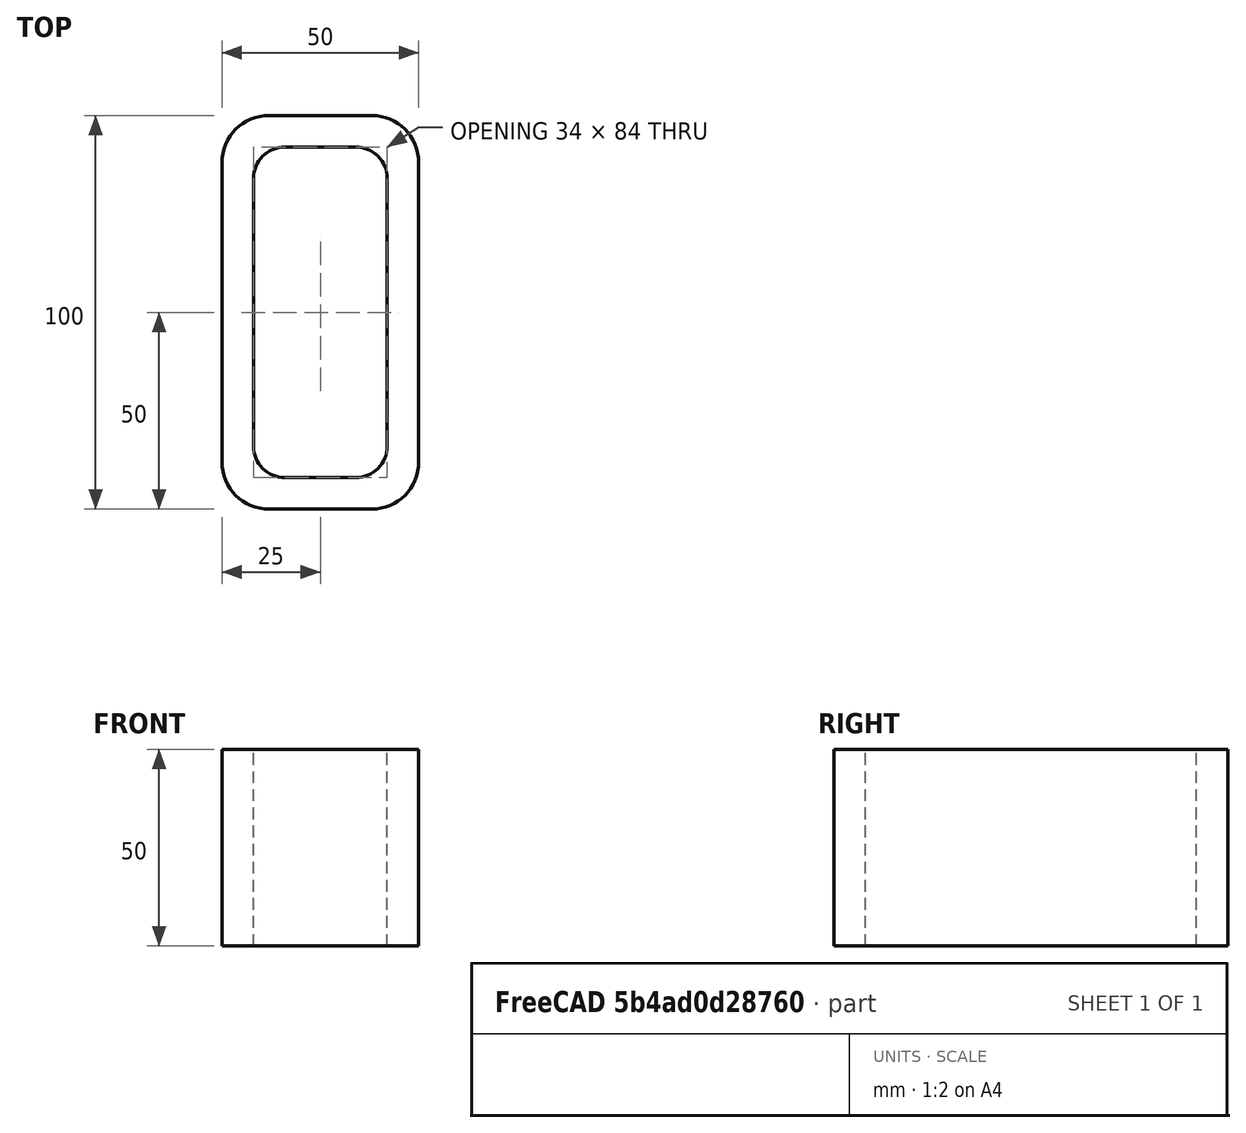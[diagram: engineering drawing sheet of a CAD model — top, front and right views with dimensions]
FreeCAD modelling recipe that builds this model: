
FCSTD DOCUMENT  (FreeCAD 0.15R4671 (Git))
Label: Rectangular hollow section 100x50x8 EN10219 S235JRH
License: All rights reserved
LicenseURL: http://en.wikipedia.org/wiki/All_rights_reserved
objects: Sketcher::SketchObject×1, Part::Extrusion×1
note: 2 computed .brp shape members not serialized (recipe doc carries the construction recipe); baked Part::Feature solids carry a one-line shape summary decoded from their .brp

FEATURE [Sketcher::SketchObject] Sketch
  sketch-geometry (16):
    g0: LineSegment StartX=-9 StartY=42 StartZ=0 EndX=9 EndY=42 EndZ=0
    g1: LineSegment StartX=17 StartY=34 StartZ=0 EndX=17 EndY=-34 EndZ=0
    g2: LineSegment StartX=9 StartY=-42 StartZ=0 EndX=-9 EndY=-42 EndZ=0
    g3: LineSegment StartX=-17 StartY=-34 StartZ=0 EndX=-17 EndY=34 EndZ=0
    g4: LineSegment StartX=-13 StartY=50 StartZ=0 EndX=13 EndY=50 EndZ=0
    g5: LineSegment StartX=25 StartY=38 StartZ=0 EndX=25 EndY=-38 EndZ=0
    g6: LineSegment StartX=13 StartY=-50 StartZ=0 EndX=-13 EndY=-50 EndZ=0
    g7: LineSegment StartX=-25 StartY=-38 StartZ=0 EndX=-25 EndY=38 EndZ=0
    g8: ArcOfCircle CenterX=-9 CenterY=34 CenterZ=0 NormalX=0 NormalY=0 NormalZ=1 Radius=8 StartAngle=1.5708 EndAngle=3.14159
    g9: ArcOfCircle CenterX=9 CenterY=34 CenterZ=0 NormalX=0 NormalY=0 NormalZ=1 Radius=8 StartAngle=0 EndAngle=1.5708
    g10: ArcOfCircle CenterX=9 CenterY=-34 CenterZ=0 NormalX=0 NormalY=0 NormalZ=1 Radius=8 StartAngle=4.71239 EndAngle=6.28319
    g11: ArcOfCircle CenterX=-9 CenterY=-34 CenterZ=0 NormalX=0 NormalY=0 NormalZ=1 Radius=8 StartAngle=3.14159 EndAngle=4.71239
    g12: ArcOfCircle CenterX=13 CenterY=38 CenterZ=0 NormalX=0 NormalY=0 NormalZ=1 Radius=12 StartAngle=0 EndAngle=1.5708
    g13: ArcOfCircle CenterX=13 CenterY=-38 CenterZ=0 NormalX=0 NormalY=0 NormalZ=1 Radius=12 StartAngle=4.71239 EndAngle=6.28319
    g14: ArcOfCircle CenterX=-13 CenterY=-38 CenterZ=0 NormalX=0 NormalY=0 NormalZ=1 Radius=12 StartAngle=3.14159 EndAngle=4.71239
    g15: ArcOfCircle CenterX=-13 CenterY=38 CenterZ=0 NormalX=0 NormalY=0 NormalZ=1 Radius=12 StartAngle=1.5708 EndAngle=3.14159
  constraints (36):
    c: Horizontal(g2)
    c: Vertical(g3)
    c: Horizontal(g6)
    c: Vertical(g7)
    c: Tangent(g3,g8) = 1.5708
    c: Tangent(g0,g8) = 1.5708
    c: Tangent(g0,g9) = 1.5708
    c: Tangent(g1,g9) = 1.5708
    c: Tangent(g1,g10) = 1.5708
    c: Tangent(g2,g10) = 1.5708
    c: Tangent(g2,g11) = 1.5708
    c: Tangent(g3,g11) = 1.5708
    c: Tangent(g4,g12) = 1.5708
    c: Tangent(g5,g12) = 1.5708
    c: Tangent(g5,g13) = 1.5708
    c: Tangent(g6,g13) = 1.5708
    c: Tangent(g6,g14) = 1.5708
    c: Tangent(g7,g14) = 1.5708
    c: Tangent(g7,g15) = 1.5708
    c: Tangent(g4,g15) = 1.5708
    c: Equal(g9,g8)
    c: Equal(g9,g11)
    c: Equal(g9,g10)
    c: Equal(g12,g15)
    c: Equal(g12,g14)
    c: Equal(g12,g13)
    c: Symmetric(g4,g6,g-1)
    c: Symmetric(g7,g5,g-2)
    c: DistanceY(g4,g6) = -100
    c: DistanceX(g7,g5) = 50
    c: Symmetric(g3,g1,g-2)
    c: Symmetric(g0,g2,g-1)
    c: DistanceY(g0,g4) = 8
    c: DistanceX(g5,g1) = -8
    c: Radius(g9) = 8
    c: Radius(g12) = 12
FEATURE [Part::Extrusion] Extrude  label="Rectangular hollow section 100x50x8 EN10219 S235JRH"
  Base = -> Sketch
  Dir = (0,0,50)
  Solid = true
